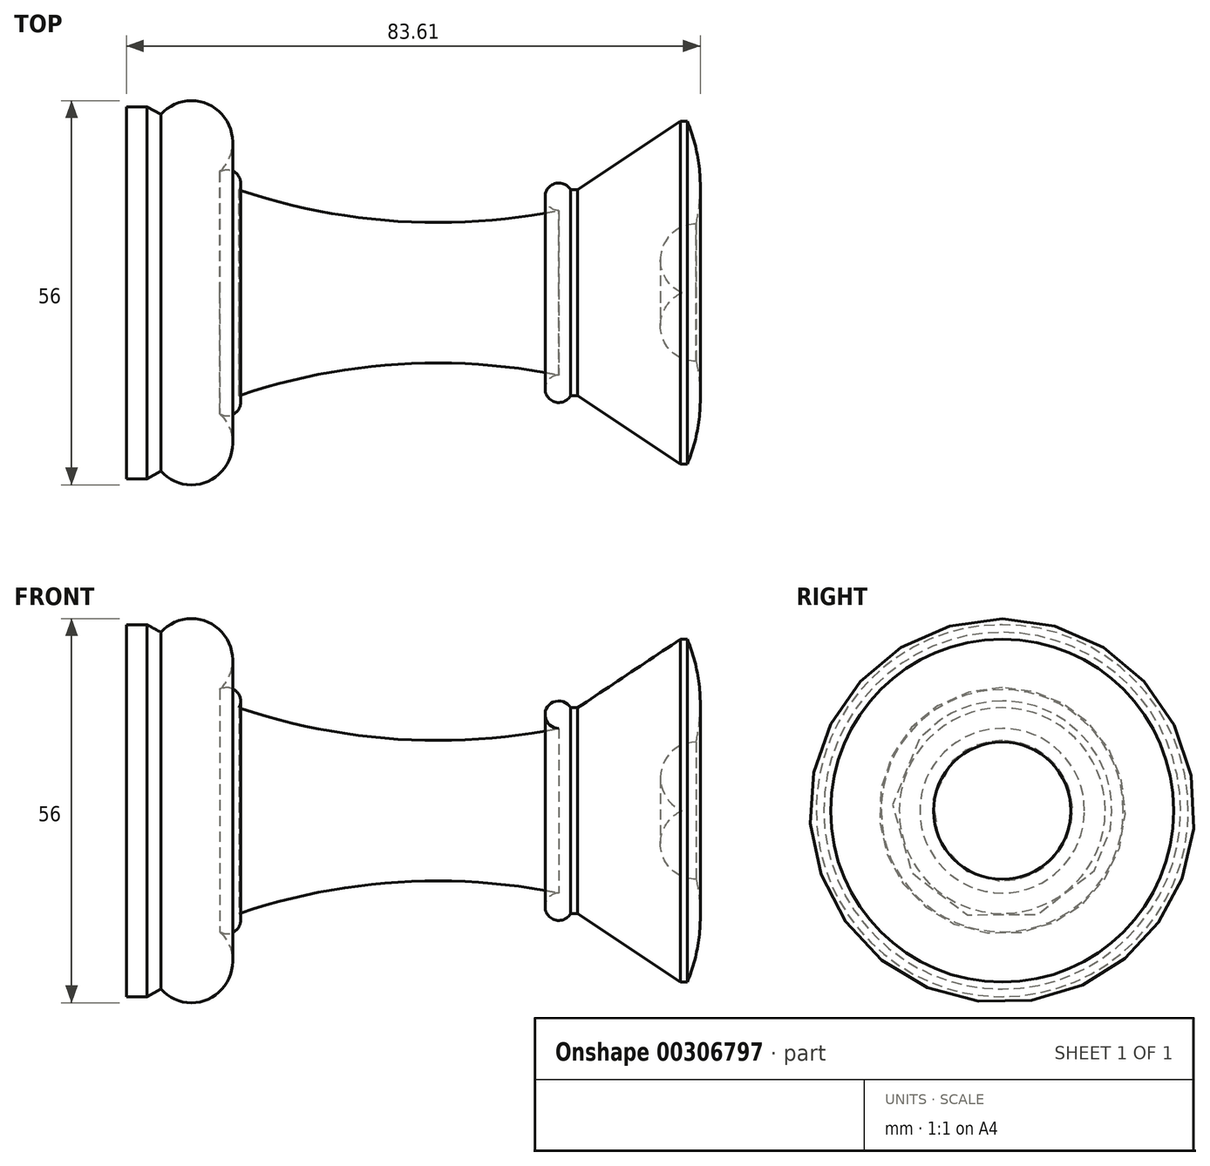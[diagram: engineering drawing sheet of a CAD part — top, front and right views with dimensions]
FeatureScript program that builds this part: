
annotation { "Feature Type Name" : "Feature", "Feature Type Description" : "" }
export const myFeature = defineFeature(function(context is Context, id is Id, definition is map)
    precondition{}
    {
        {
            var Q0;
            Q0=qCreatedBy(makeId("Front.planeOp"),FACE);
            var sketch = newSketch(context, id + "F0", { "sketchPlane" : qUnion([Q0])});
            skArc(sketch, "E0", {"start": v(-2, -10) * mm, "mid": v(3.1, -5.82) * mm, "end": v(0, 0) * mm});
            skArc(sketch, "E1", {"start": v(-3.27, -25) * mm, "mid": v(-1.48, -17.6) * mm, "end": v(-2, -10) * mm});
            skLineSegment(sketch, "E2", {"start": v(-3.27, -25) * mm, "end": v(-4.27, -25) * mm});
            skLineSegment(sketch, "E3", {"start": v(-4.27, -25) * mm, "end": v(-19.27, -15) * mm});
            skLineSegment(sketch, "E4", {"start": v(-19.27, -15) * mm, "end": v(-20.27, -15) * mm});
            skArc(sketch, "E5", {"start": v(-22, -12) * mm, "mid": v(-23.73, -15) * mm, "end": v(-20.27, -15) * mm});
            skArc(sketch, "E6", {"start": v(-22, -12) * mm, "mid": v(-45.5, -10.43) * mm, "end": v(-68.59, -15) * mm});
            skArc(sketch, "E7", {"start": v(-71.55, -17.54) * mm, "mid": v(-69.05, -17.46) * mm, "end": v(-68.59, -15) * mm});
            skLineSegment(sketch, "E8", {"start": v(-71.55, -17.54) * mm, "end": v(-72.55, -16.79) * mm});
            skArc(sketch, "E9", {"start": v(-80, -26) * mm, "mid": v(-70.86, -25.77) * mm, "end": v(-72.55, -16.79) * mm});
            skLineSegment(sketch, "E10", {"start": v(-80, -26) * mm, "end": v(-82, -27.11) * mm});
            skLineSegment(sketch, "E11", {"start": v(-82, -27.11) * mm, "end": v(-85, -27.11) * mm});
            skLineSegment(sketch, "E12", {"start": v(-85, -27.11) * mm, "end": v(-85, 0) * mm});
            skLineSegment(sketch, "E13", {"start": v(-85, 0) * mm, "end": v(0, 0) * mm});
            skSolve(sketch);
        }
        {
            var Q0;
            Q0 = qSketchRegion(id + "F0", true);
            var Q1;
            Q1=sQuery(id+"F0.wireOp",EDGE,"E13");
            revolve(context, id + "F1", {"entities" : qUnion([Q0]), "axis" : qUnion([Q1]), "revolveType" : RevolveType.FULL});
        }
    });
